# Revit family: Rough_In_Valve-GROHE-28672000
name_source: partatom
category: Plumbing Fixtures
revit_build: Autodesk Revit 2014 (Build: 20130308_1515(x64)
units: mm (PartAtom-declared; Revit-internal decimal feet)

## types (1)
- 28672000
    Assembly Code = D2020
    CW Connection = Yes
    CWFU = 2
    Connection Diameter = 1/2"
    Default Elevation = 68"
    Description = Relexa Shower Outlet Elbow.
    Finish = Brass-Grohe-000-Starlight Chrome
    HW Connection = Yes
    HWFU = 3
    Height = 2 3/4"
    Installation Type = Wall Mounted
    Length = 2 5/8"
    Manufacturer = GROHE
    Material = Brass-Grohe-000-Starlight Chrome
    Model = 28672000
    Price = Prices may vary. Please consult Manufacturer Representative for most up-to-date price list.
    Product Page URL = http://www.grohe.com
    Shipping Weight = 0.310 lb
    URL = http://www.grohe.com
    Vent Connection = No
    WFU = 4
    Warranty Information = Limited Lifetime Warranty
    Waste Connection = No
    Width = 2 5/8"

## geometry (parser evidence)
native form markers: Sweep x3
no freeform markers — native parametric forms only
